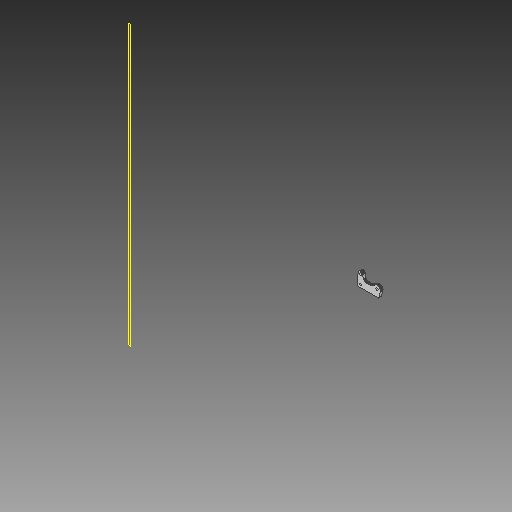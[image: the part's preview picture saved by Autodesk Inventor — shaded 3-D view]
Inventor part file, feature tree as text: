
AUTODESK INVENTOR PART (.ipt)
format: ipt  version: 2017 (Build 210142000, 142)  size: 304,640 bytes
history: native  units: mm
features: other x3, sketch x2, plane x1
ambient origin geometry x8: Origin, YZ Plane, XZ Plane, XY Plane, X Axis, Y Axis, Z Axis, Center Point
bodies: Solid1 (feature_tree)
feature tree (6):
  other  "X-Idler.ipt"
  other  "Solid1::X-Idler.ipt"
  other  "TaggingFeature1"
  sketch  "Sketch1"  dims[d0=10.0mm]
  sketch  "Sketch2"
  plane  "Work Plane1"
